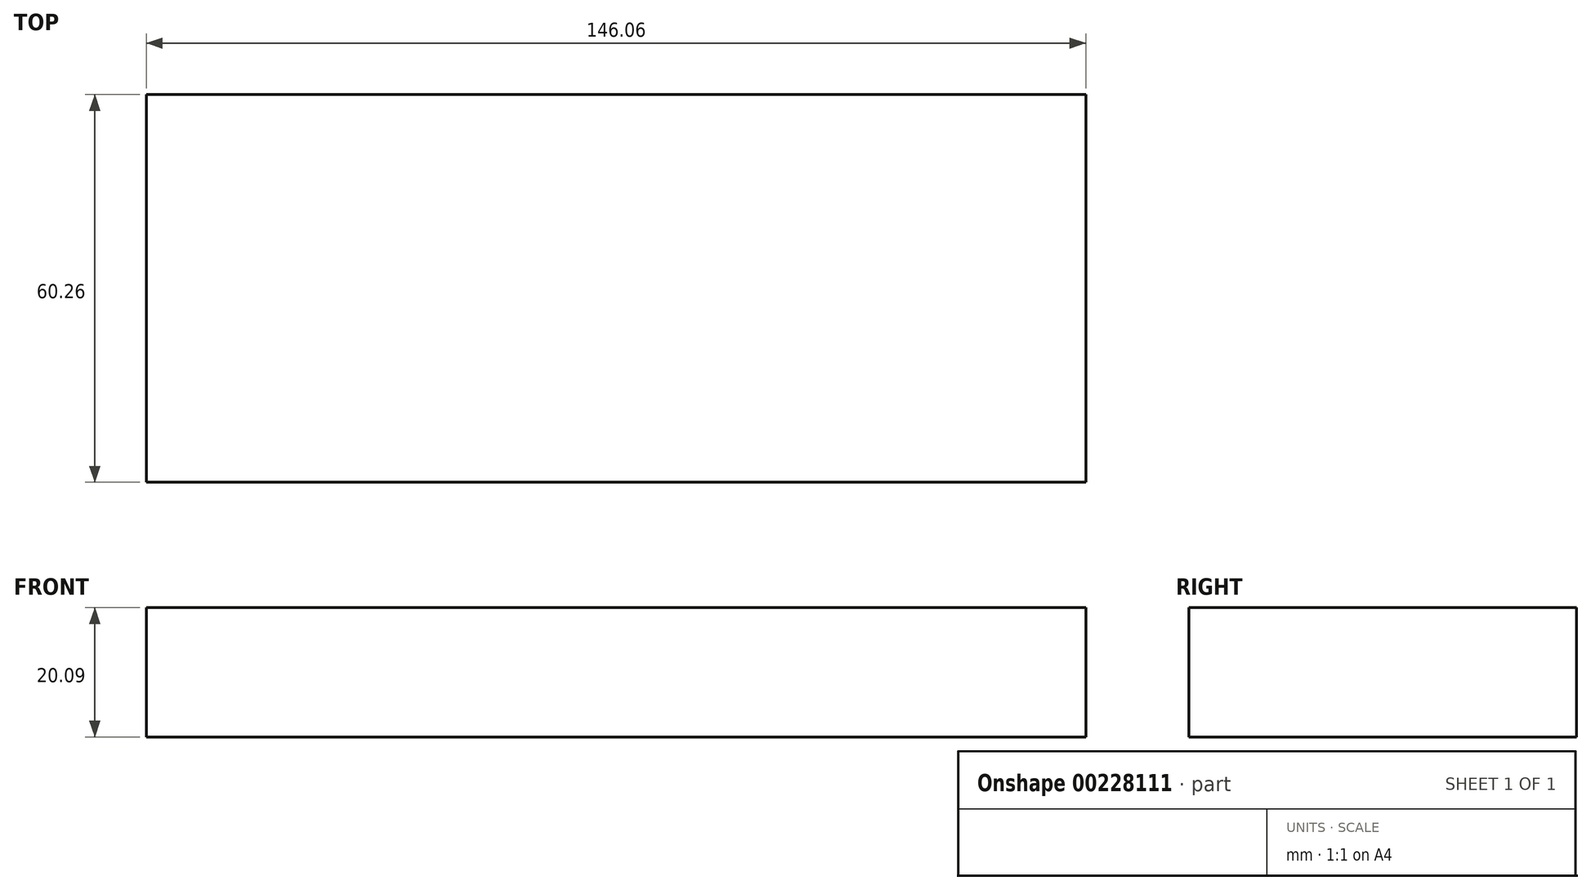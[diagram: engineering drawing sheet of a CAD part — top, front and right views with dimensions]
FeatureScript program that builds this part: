
annotation { "Feature Type Name" : "Feature", "Feature Type Description" : "" }
export const myFeature = defineFeature(function(context is Context, id is Id, definition is map)
    precondition{}
    {
        {
            var Q0;
            Q0=qCreatedBy(makeId("Top.planeOp"),FACE);
            var sketch = newSketch(context, id + "F0", { "sketchPlane" : qUnion([Q0])});
            skLineSegment(sketch, "E0.bottom", {"start": v(73.03, -30.13) * mm, "end": v(-73.03, -30.13) * mm});
            skLineSegment(sketch, "E0.top", {"start": v(73.03, 30.13) * mm, "end": v(-73.03, 30.13) * mm});
            skLineSegment(sketch, "E0.left", {"start": v(73.03, -30.13) * mm, "end": v(73.03, 30.13) * mm});
            skLineSegment(sketch, "E0.right", {"start": v(-73.03, -30.13) * mm, "end": v(-73.03, 30.13) * mm});
            skPoint(sketch, "E0.middle", {"position": v(0, 0) * mm});
            skSolve(sketch);
        }
        {
            var Q0;
            Q0 = qSketchRegion(id + "F0", true);
            extrude(context, id + "F1", {"entities" : qUnion([Q0]), "depth" : 20.1 * mm});
        }
    });
